# Revit family: 18460-presto
name_source: partatom
category: Plumbing Fixtures
units: mm (PartAtom-declared; Revit-internal decimal feet)

## family parameters
Always vertical = Yes
Cut with Voids When Loaded = No
Maintain Annotation Orientation = No
OmniClass Number = 23.45.00.00
OmniClass Title = Sanitary, Laundry, and Cleaning Equipment
Part Type = Normal
Room Calculation Point = No
Round Connector Dimension = Use Diameter
Shared = No
Work Plane-Based = Yes

## types (1)
- 18460 - presto
    Assembly Code = 18460
    Default Elevation = 1219 mm
    Description = Self-supporting mounting frame with PRESTO 7100 XL N
    Manufacturer = presto
    Recommended pressure = 3 bar
    URL = https://www.prestodatashare.com
    brand = LES ROBINETS PRESTO
    flow = 6.0 L/s
    flow time = 1.0 s
    material = 60 micron epoxy coated soldered steel mounting frame / - Galvanized legs and floor fixing plates / - Brass body flush valve / - Anti-vandal brushed stainless steel 304L front plate
    min flow = 1.0 L/s
    min pressure = 1 bar
    power = 0 W
    pressure = 5 bar
    range = SELF-SUPPORTING MOUTING FRAME WITH DIRECT FLUSH
    ref = 18460 - Self-supporting mounting frame with PRESTO 7100 XL N

## geometry (parser evidence)
native form markers: Sweep x1
no freeform markers — native parametric forms only
